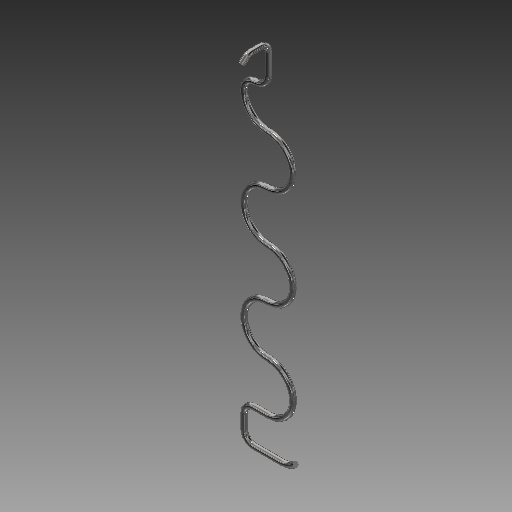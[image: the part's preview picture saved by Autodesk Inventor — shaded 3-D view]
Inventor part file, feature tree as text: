
AUTODESK INVENTOR PART (.ipt)
format: ipt  version: 2019 (Build 230136000, 136)  size: 169,984 bytes
history: native  units: mm
features: sketch x4, sweep x2, plane x1, other x1
ambient origin geometry x8: Origin, YZ Plane, XZ Plane, XY Plane, X Axis, Y Axis, Z Axis, Center Point
bodies: Solid1 (feature_tree)
feature tree (8):
  sketch  "Sketch1"  dims[d1=5.0mm d2=6.108652mm]
  plane  "Work Plane1"
  sweep  "Sweep2"
  sweep  "Sweep3"
  other  "Work Axis1"
  sketch  "Sketch2"  dims[d3=25.0mm d5=8.0mm]
  sketch  "Sketch3"  dims[d6=18.0mm]
  sketch  "Sketch4"  dims[d7=15.0mm d8=4.0mm d10=36.0mm d11=36.0mm d13=36.0mm d15=36.0mm d17=18.0mm d18=9.0mm d19=151.0mm d20=223.0mm d21=9.0mm d22=18.0mm d23=9.0mm d24=0.0mm d25=15.0mm d26=15.0mm d27=6.981317mm d28=5.0mm d29=6.0mm d30=0.0mm d31=0.0mm d32=0.0mm]
